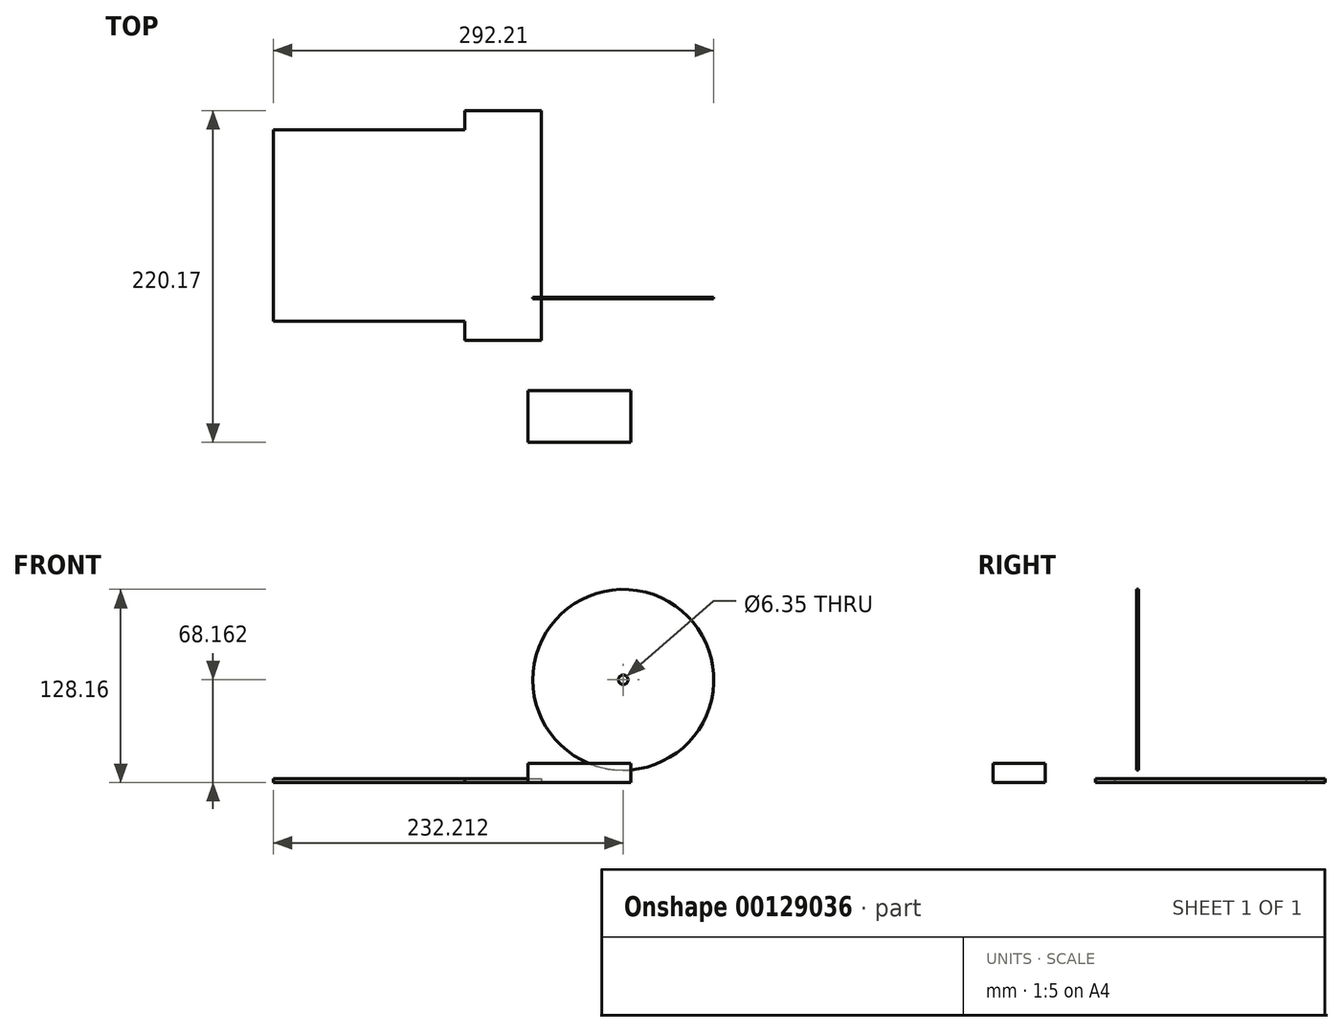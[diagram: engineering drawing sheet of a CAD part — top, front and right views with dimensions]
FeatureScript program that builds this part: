
annotation { "Feature Type Name" : "Feature", "Feature Type Description" : "" }
export const myFeature = defineFeature(function(context is Context, id is Id, definition is map)
    precondition{}
    {
        {
            var Q0;
            Q0=qCreatedBy(makeId("Top.planeOp"),FACE);
            var sketch = newSketch(context, id + "F0", { "sketchPlane" : qUnion([Q0])});
            skLineSegment(sketch, "E0.bottom", {"start": v(-127, 111.05) * mm, "end": v(0, 111.05) * mm});
            skLineSegment(sketch, "E0.top", {"start": v(-127, -15.95) * mm, "end": v(0, -15.95) * mm});
            skLineSegment(sketch, "E0.left", {"start": v(-127, 111.05) * mm, "end": v(-127, -15.95) * mm});
            skLineSegment(sketch, "E0.right", {"start": v(0, 111.05) * mm, "end": v(0, -15.95) * mm});
            skLineSegment(sketch, "E1.bottom", {"start": v(0, 123.75) * mm, "end": v(50.8, 123.75) * mm});
            skLineSegment(sketch, "E1.top", {"start": v(0, -28.65) * mm, "end": v(50.8, -28.65) * mm});
            skLineSegment(sketch, "E1.left", {"start": v(0, 123.75) * mm, "end": v(0, -28.65) * mm});
            skLineSegment(sketch, "E1.right", {"start": v(50.8, 123.75) * mm, "end": v(50.8, -28.65) * mm});
            skSolve(sketch);
        }
        {
            var Q0;
            {var subQ0=sQuery(id+"F0.wireOp",EDGE,"E0.bottom");Q0=makeQuery(id+"F0.imprint","IMPRINT",FACE,{"disambiguationData":[TD([[makeQuery(id+"F0.imprint","IMPRINT",EDGE,{"derivedFrom":subQ0}),-1.0]])]});}
            var Q1;
            {var subQ3=sQuery(id+"F0.wireOp",EDGE,"E1.bottom");Q1=makeQuery(id+"F0.imprint","IMPRINT",FACE,{"disambiguationData":[TD([[makeQuery(id+"F0.imprint","IMPRINT",EDGE,{"derivedFrom":subQ3}),-1.0]])]});}
            extrude(context, id + "F1", {"entities" : qUnion([Q0, Q1]), "depth" : 2.54 * mm});
        }
        {
            var Q0;
            Q0=qCreatedBy(makeId("Front.planeOp"),FACE);
            var sketch = newSketch(context, id + "F2", { "sketchPlane" : qUnion([Q0])});
            skCircle(sketch, "E2", {"center": v(105.21, 68.16) * mm, "radius": 60 * mm});
            skCircle(sketch, "E3", {"center": v(105.21, 68.16) * mm, "radius": 3.18 * mm});
            skSolve(sketch);
        }
        {
            var Q0;
            Q0=makeQuery(id+"F2.imprint","IMPRINT",FACE,{"disambiguationData":[TD([[makeQuery(id+"F2.imprint","IMPRINT",EDGE,{"derivedFrom":sQuery(id+"F2.wireOp",EDGE,"E2")}),1.0]])]});
            extrude(context, id + "F3", {"entities" : qUnion([Q0]), "operationType" : NewBodyOperationType.ADD, "depth" : 1.2 * mm});
        }
        {
            var Q0;
            Q0=qCreatedBy(makeId("Top.planeOp"),FACE);
            var sketch = newSketch(context, id + "F4", { "sketchPlane" : qUnion([Q0])});
            skLineSegment(sketch, "E4.bottom", {"start": v(42, -62.08) * mm, "end": v(110.1, -62.08) * mm});
            skLineSegment(sketch, "E4.top", {"start": v(42, -96.42) * mm, "end": v(110.1, -96.42) * mm});
            skLineSegment(sketch, "E4.left", {"start": v(42, -62.08) * mm, "end": v(42, -96.42) * mm});
            skLineSegment(sketch, "E4.right", {"start": v(110.1, -62.08) * mm, "end": v(110.1, -96.42) * mm});
            skSolve(sketch);
        }
        {
            var Q0;
            Q0=makeQuery(id+"F4.imprint","IMPRINT",FACE,{"disambiguationData":[TD([[makeQuery(id+"F4.imprint","IMPRINT",EDGE,{"derivedFrom":sQuery(id+"F4.wireOp",EDGE,"E4.bottom")}),-1.0]])]});
            extrude(context, id + "F5", {"entities" : qUnion([Q0]), "depth" : 12.7 * mm});
        }
    });
